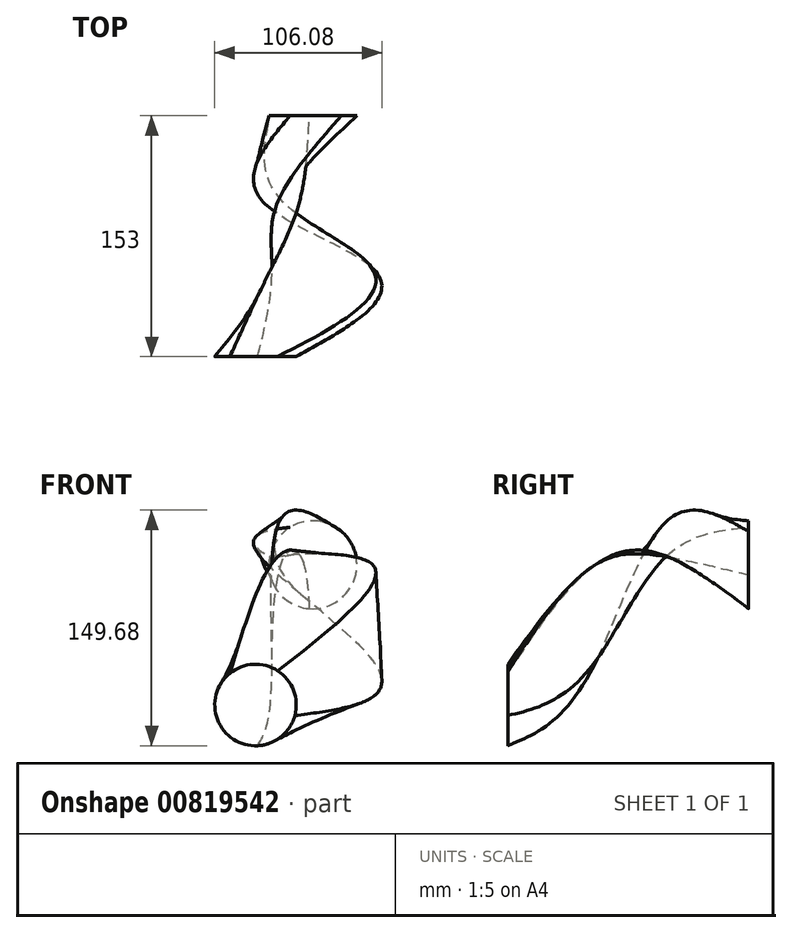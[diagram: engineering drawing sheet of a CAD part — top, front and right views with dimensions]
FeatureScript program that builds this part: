
annotation { "Feature Type Name" : "Feature", "Feature Type Description" : "" }
export const myFeature = defineFeature(function(context is Context, id is Id, definition is map)
    precondition{}
    {
        {
            var Q0;
            Q0=qCreatedBy(makeId("Front.planeOp"),FACE);
            cPlane(context, id + "F0", {"entities" : qUnion([Q0]), "cplaneType" : CPlaneType.OFFSET, "offset" : 53 * mm, "width" : 150 * mm, "height" : 150 * mm});
        }
        {
            var Q0;
            Q0=qCreatedBy(makeId("Front.planeOp"),FACE);
            cPlane(context, id + "F1", {"entities" : qUnion([Q0]), "cplaneType" : CPlaneType.OFFSET, "offset" : 96 * mm, "width" : 150 * mm, "height" : 150 * mm});
        }
        {
            var Q0;
            Q0=qCreatedBy(makeId("Front.planeOp"),FACE);
            cPlane(context, id + "F2", {"entities" : qUnion([Q0]), "cplaneType" : CPlaneType.OFFSET, "offset" : 153 * mm, "width" : 150 * mm, "height" : 150 * mm});
        }
        {
            var Q0;
            Q0=qCreatedBy(id+"F2.planeOp",FACE);
            var sketch = newSketch(context, id + "F3", { "sketchPlane" : qUnion([Q0])});
            skCircle(sketch, "E0", {"center": v(-40.2, -44) * mm, "radius": 25.88 * mm});
            skPoint(sketch, "E1", {"position": v(-42.44, -56.56) * mm});
            skPoint(sketch, "E2", {"position": v(-64.36, -53.28) * mm});
            skSolve(sketch);
        }
        {
            var Q0;
            Q0=qCreatedBy(id+"F1.planeOp",FACE);
            var sketch = newSketch(context, id + "F4", { "sketchPlane" : qUnion([Q0])});
            skLineSegment(sketch, "E3.bottom", {"start": v(-29.75, 45.95) * mm, "end": v(33.25, 45.95) * mm});
            skLineSegment(sketch, "E3.top", {"start": v(-29.75, -14.4) * mm, "end": v(33.25, -14.4) * mm});
            skLineSegment(sketch, "E3.left", {"start": v(-29.75, 45.95) * mm, "end": v(-29.75, -14.4) * mm});
            skLineSegment(sketch, "E3.right", {"start": v(33.25, 45.95) * mm, "end": v(33.25, -14.4) * mm});
            skPoint(sketch, "E4", {"position": v(-29.75, 0) * mm});
            skSolve(sketch);
        }
        {
            var Q0;
            Q0=qCreatedBy(id+"F0.planeOp",FACE);
            var sketch = newSketch(context, id + "F5", { "sketchPlane" : qUnion([Q0])});
            skCircle(sketch, "E5.cCircle", {"center": v(-24.67, 57.48) * mm, "radius": 7.2 * mm, "construction": true});
            skLineSegment(sketch, "E5.0", {"start": v(-25.34, 71.87) * mm, "end": v(-11.87, 50.86) * mm});
            skLineSegment(sketch, "E5.1", {"start": v(-11.87, 50.86) * mm, "end": v(-36.8, 49.7) * mm});
            skLineSegment(sketch, "E5.2", {"start": v(-36.8, 49.7) * mm, "end": v(-25.34, 71.87) * mm});
            skPoint(sketch, "E5.0.midPoint", {"position": v(-18.6, 61.37) * mm});
            skPoint(sketch, "E6", {"position": v(-22.45, 67.36) * mm});
            skSolve(sketch);
        }
        {
            var Q0;
            Q0=qCreatedBy(makeId("Front.planeOp"),FACE);
            var sketch = newSketch(context, id + "F6", { "sketchPlane" : qUnion([Q0])});
            skCircle(sketch, "E7", {"center": v(-3.78, 45.06) * mm, "radius": 27.92 * mm});
            skPoint(sketch, "E8", {"position": v(0, 31.38) * mm});
            skPoint(sketch, "E9", {"position": v(21.98, 34.27) * mm});
            skSolve(sketch);
        }
        {
            var Q0;
            Q0=makeQuery(id+"F3.imprint","IMPRINT",FACE,{"disambiguationData":[TD([[makeQuery(id+"F3.imprint","IMPRINT",EDGE,{"derivedFrom":sQuery(id+"F3.wireOp",EDGE,"E0")}),1.0]])]});
            var Q1;
            Q1=makeQuery(id+"F4.imprint","IMPRINT",FACE,{"disambiguationData":[TD([[makeQuery(id+"F4.imprint","IMPRINT",EDGE,{"derivedFrom":sQuery(id+"F4.wireOp",EDGE,"E3.bottom")}),-1.0]])]});
            var Q2;
            Q2=makeQuery(id+"F5.imprint","IMPRINT",FACE,{"disambiguationData":[TD([[makeQuery(id+"F5.imprint","IMPRINT",EDGE,{"derivedFrom":sQuery(id+"F5.wireOp",EDGE,"E5.0")}),-1.0]])]});
            var Q3;
            Q3=makeQuery(id+"F6.imprint","IMPRINT",FACE,{"disambiguationData":[TD([[makeQuery(id+"F6.imprint","IMPRINT",EDGE,{"derivedFrom":sQuery(id+"F6.wireOp",EDGE,"E7")}),1.0]])]});
            var Q4;
            Q4=sQuery(id+"F3.wireOp",VERTEX,"E2");
            var Q5;
            Q5=sQuery(id+"F4.wireOp",VERTEX,"E4");
            var Q6;
            Q6=sQuery(id+"F5.wireOp",VERTEX,"E6");
            var Q7;
            Q7=sQuery(id+"F6.wireOp",VERTEX,"E9");
            loft(context, id + "F7", {"sheetProfilesArray" : [{ "sheetProfileEntities" : qUnion([Q0]) }, { "sheetProfileEntities" : qUnion([Q1]) }, { "sheetProfileEntities" : qUnion([Q2]) }, { "sheetProfileEntities" : qUnion([Q3]) }], "matchConnections" : true, "connections" : [{ "connectionEntities" : qUnion([Q4, Q5, Q6, Q7]), "connectionEdgeQueries" : qUnion([]), "connectionEdgeParameters" : [] }]});
        }
    });
